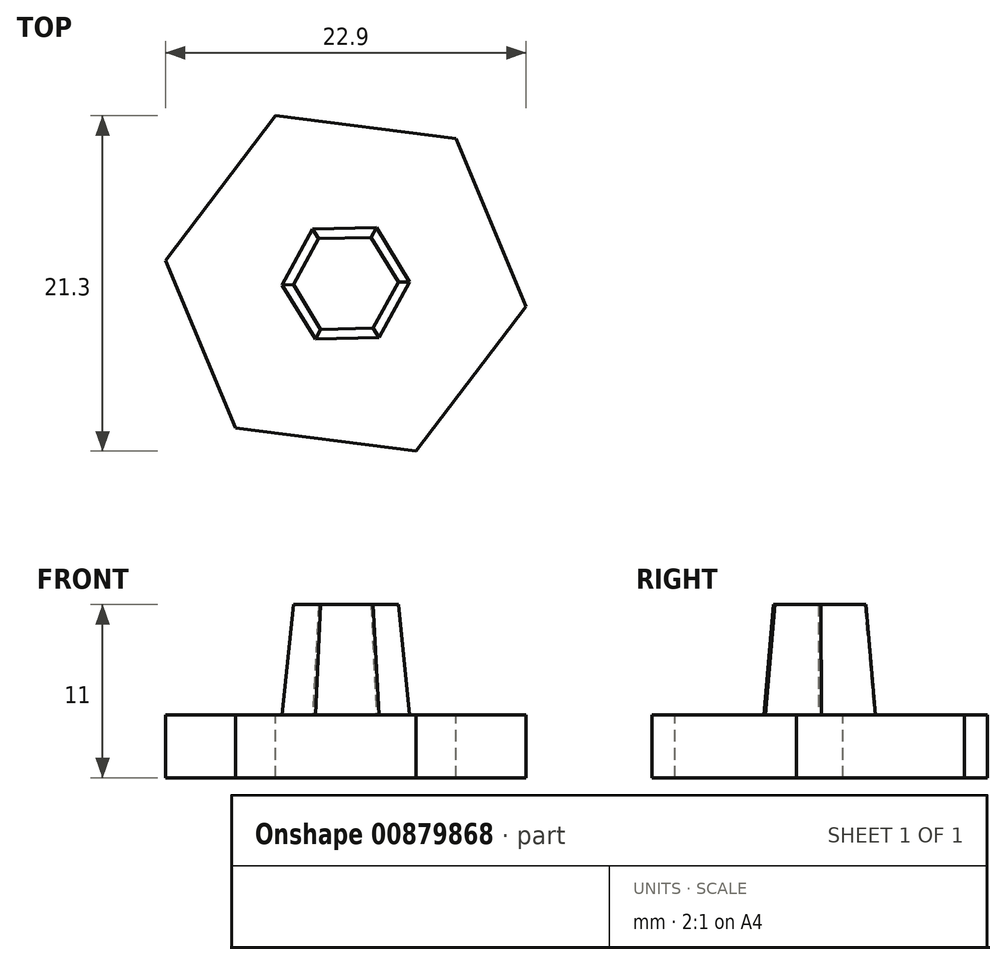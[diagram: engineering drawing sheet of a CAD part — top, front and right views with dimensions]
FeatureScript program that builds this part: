
annotation { "Feature Type Name" : "Feature", "Feature Type Description" : "" }
export const myFeature = defineFeature(function(context is Context, id is Id, definition is map)
    precondition{}
    {
        {
            var Q0;
            Q0=qCreatedBy(makeId("Top.planeOp"),FACE);
            var sketch = newSketch(context, id + "F0", { "sketchPlane" : qUnion([Q0])});
            skCircle(sketch, "E0.cCircle", {"center": v(0, 0) * mm, "radius": 3.5 * mm, "construction": true});
            skLineSegment(sketch, "E0.0", {"start": v(4.04, 0.1) * mm, "end": v(2.1, -3.45) * mm});
            skLineSegment(sketch, "E0.1", {"start": v(2.1, -3.45) * mm, "end": v(-1.94, -3.55) * mm});
            skLineSegment(sketch, "E0.2", {"start": v(-1.94, -3.55) * mm, "end": v(-4.04, -0.1) * mm});
            skLineSegment(sketch, "E0.3", {"start": v(-4.04, -0.1) * mm, "end": v(-2.1, 3.45) * mm});
            skLineSegment(sketch, "E0.4", {"start": v(-2.1, 3.45) * mm, "end": v(1.94, 3.55) * mm});
            skLineSegment(sketch, "E0.5", {"start": v(1.94, 3.55) * mm, "end": v(4.04, 0.1) * mm});
            skPoint(sketch, "E0.0.midPoint", {"position": v(3.07, -1.68) * mm});
            skCircle(sketch, "E1.cCircle", {"center": v(0, 0) * mm, "radius": 10 * mm, "construction": true});
            skLineSegment(sketch, "E1.0", {"start": v(11.45, -1.47) * mm, "end": v(4.46, -10.65) * mm});
            skLineSegment(sketch, "E1.1", {"start": v(4.46, -10.65) * mm, "end": v(-7, -9.18) * mm});
            skLineSegment(sketch, "E1.2", {"start": v(-7, -9.18) * mm, "end": v(-11.45, 1.47) * mm});
            skLineSegment(sketch, "E1.3", {"start": v(-11.45, 1.47) * mm, "end": v(-4.46, 10.65) * mm});
            skLineSegment(sketch, "E1.4", {"start": v(-4.46, 10.65) * mm, "end": v(7, 9.18) * mm});
            skLineSegment(sketch, "E1.5", {"start": v(7, 9.18) * mm, "end": v(11.45, -1.47) * mm});
            skPoint(sketch, "E1.0.midPoint", {"position": v(7.95, -6.06) * mm});
            skSolve(sketch);
        }
        {
            var Q0;
            Q0=makeQuery(id+"F0.imprint","IMPRINT",FACE,{"disambiguationData":[TD([[makeQuery(id+"F0.imprint","IMPRINT",EDGE,{"derivedFrom":sQuery(id+"F0.wireOp",EDGE,"E0.0")}),-1.0]])]});
            extrude(context, id + "F1", {"entities" : qUnion([Q0]), "depth" : 7 * mm, "offsetDistance" : 25 * mm, "hasDraft" : true, "draftAngle" : 5 * degree, "draftPullDirection" : true, "hasSecondDirection" : true, "secondDirectionOppositeDirection" : true, "secondDirectionDepth" : 4 * mm});
        }
        {
            var Q0;
            Q0=makeQuery(id+"F0.imprint","IMPRINT",FACE,{"disambiguationData":[TD([[makeQuery(id+"F0.imprint","IMPRINT",EDGE,{"derivedFrom":sQuery(id+"F0.wireOp",EDGE,"E0.0")}),1.0]])]});
            extrude(context, id + "F2", {"entities" : qUnion([Q0]), "operationType" : NewBodyOperationType.ADD, "oppositeDirection" : true, "depth" : 4 * mm, "offsetDistance" : 25 * mm});
        }
    });
